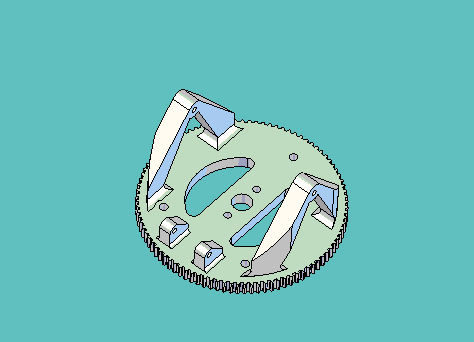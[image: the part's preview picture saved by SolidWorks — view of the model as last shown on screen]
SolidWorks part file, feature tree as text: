
SOLIDWORKS PART (.sldprt)
format: sldprt  version: not decoded by parser v0  size: 2,464,768 bytes
history: native  units: mm
features: sketch x18, cut_extrude x11, extrude x7, plane x7, fillet x3, material x1 (+11 scaffold rows collapsed)
feature tree (58):
  scaffold x11  (default folders/planes/origin — collapsed)
  material  "Material <not specified>"
  sketch  "Sketch1"  dims[c1.D1=50.8mm c1.D7=3.175mm c2.D1=89.1032mm c2.D2=~93.32036mm c3.D2=45.0deg c3.D3=~94.913632mm c4.D3=45.0deg c4.D4=6.35mm c4.D5=6.35mm c4.D6=31.75mm]
  extrude  "Extrude1"  Depth=6.35mm
  sketch  "Sketch2"  dims[c1.D1=50.8mm c1.D7=~3.96875mm c2.D1=~3.96875mm c2.D4=~3.96875mm c2.D2=~93.32036mm c3.D2=163.0deg c3.D3=~94.913632mm c4.D3=45.0deg c4.D4=4.7625mm c4.D5=4.7625mm c4.D6=31.75mm c4.D1=4.7625mm c5.D6=34.925mm]
  cut_extrude  "Cut-Extrude8"  [1 undecoded]
  sketch  "Sketch3"  dims[D1=3.4544mm D2=3.4544mm D3=9.525mm]
  cut_extrude  "Cut-Extrude2"  [1 undecoded]
  sketch  "Sketch5"  dims[c1.D3=19.05mm c1.D4=25.4mm c1.D1=20.6375mm c1.D2=20.6375mm c1.D5=~49.79749mm c2.D5=30.0deg c2.D6=11.1125mm c2.D1=17.145mm c2.D2=17.145mm c3.D1=~82.457251mm c4.D1=90.0deg c4.D2=9.525mm c4.D3=9.525mm]
  cut_extrude  "Cut-Extrude4"  [1 undecoded]
  fillet  "Fillet2"  Radius=3.175mm
  sketch  "Sketch6"  dims[D1=9.525mm]
  extrude  "Axis2"  [1 undecoded]
  plane  "Plane1"
  plane  "Plane2"
  plane  "Plane3"  Offset=50.8mm
  sketch  "Sketch11"  dims[c1.D1=40.3225mm c1.D2=40.3225mm c2.D1=22.86mm c2.D2=24.384mm c2.D3=30.1625mm c2.D4=30.1625mm]
  extrude  "Extrude6"  Depth=44.45mm
  sketch  "Sketch7"  dims[D1=2.7051mm D2=4.7625mm]
  cut_extrude  "Cut-Extrude7"  [1 undecoded]
  sketch  "Sketch12"  dims[D1=6.35mm D2=6.35mm D3=6.35mm]
  cut_extrude  "Cut-Extrude9"  [1 undecoded]
  sketch  "Sketch14"  dims[D1=13.97mm D2=13.97mm D3=19.7866mm]
  extrude  "Extrude7"  Depth=2.38125mm
  sketch  "Sketch13"  dims[D1=~3.571875mm D2=~3.571875mm]
  cut_extrude  "Cut-Extrude11"  [1 undecoded]
  sketch  "Sketch15"  dims[c1.D4=3.175mm c1.D1=9.525mm c1.D2=9.525mm c1.D3=9.525mm c2.D1=9.525mm c2.D2=9.525mm c2.D5=25.4mm c2.D6=25.4mm]
  cut_extrude  "Cut-Extrude12"  [1 undecoded]
  fillet  "Fillet3"  Radius=3.175mm
  sketch  "Sketch16"  dims[D1=7.9375mm D2=7.9375mm]
  cut_extrude  "Cut-Extrude13"  [1 undecoded]
  plane  "Plane4"  Offset=7.14375mm
  plane  "Plane5"  Offset=7.14375mm
  sketch  "Sketch17"  dims[c1.D4=2.7051mm c1.D1=28.575mm c1.D2=9.525mm c1.D3=6.35mm c2.D1=38.1mm c2.D5=~9.745748mm c2.D3=9.525mm c3.D5=6.35mm c3.D6=3.175mm c3.D2=~11.90625mm c4.D5=~8.73125mm c4.D7=4.7625mm]
  extrude  "Extrude8"  Depth=5.969mm
  sketch  "Sketch18"  dims[D1=0.0mm]
  extrude  "Extrude9"  Depth=5.969mm
  fillet  "Fillet5"  Radius=1.5875mm
  plane  "Plane6"  Offset=39.6875mm
  plane  "Plane7"  Offset=39.6875mm
  sketch  "Sketch19"  dims[D1=12.7mm]
  cut_extrude  "Cut-Extrude14"  [1 undecoded]
  sketch  "Sketch20"
  cut_extrude  "Cut-Extrude15"  [1 undecoded]
  sketch  "Sketch21"  dims[D1=~2.38125mm]
  cut_extrude  "Cut-Extrude16"  [1 undecoded]
  sketch  "Sketch22"  dims[c1.D1=~90.71926mm c1.D4=~45.35963mm c2.D1=~45.35963mm c2.D4=~45.35963mm c2.D5=~45.35963mm c2.D9=2.0422mm c3.D1=45.3644mm c3.D2=~55.294757mm c4.D2=30.0deg c4.D3=~55.294757mm c5.D3=30.0deg c5.D4=~45.35963mm c5.D1=~2.999484mm c6.D4=~45.35963mm c6.D5=~45.35963mm c6.D2=0.809mm c6.D3=2.41mm c6.D6=1.19mm c6.D7=0.324mm c6.D8=0.1944mm c6.D9=0.1944mm c6.D10=1.19mm c7.D2=0.381mm c7.D3=1.2192mm c7.D4=2.413mm c7.D5=0.3302mm c7.D6=~49.397463mm c8.D6=1.8947deg c8.D7=~49.397463mm c9.D7=1.8947deg c9.D8=~0.11938mm c9.D9=~0.11938mm c9.D10=~0.19558mm c9.D11=~0.19558mm c9.D4=~282.002929mm c9.D1=~282.002929mm c10.D4=3.0mm c10.D5=1.5mm c10.D2=0.8128mm]
  extrude  "Extrude10"  [1 undecoded]
decode coverage: 25 of 39 modeling features carry decoded parameters
note: ~ marks probable driven/reference dimensions
note: 13 parameter values undecoded
summary: no parameter record found for 13 features
note: suppression state not decoded; provenance and decode notes live in map.json
